# Revit family: 2M_Check Valve_UNIVAL_CHE-0601 - 125-200 mm
name_source: partatom
category: Pipe Accessories
revit_build: Autodesk Revit 2016 (Build: 20150220_1215(x64)
units: mm (PartAtom-declared; Revit-internal decimal feet)

## family parameters
Always vertical = Yes
Cut with Voids When Loaded = No
OmniClass Number = 23.65.55.14
OmniClass Title = Valves for Liquid Services
Part Type = Valve - Breaks Into
Round Connector Dimension = Use Diameter
Shared = No
Work Plane-Based = No

## types (3) — shared parameters
Body Material = Ductile iron / Stainless steel (GGG50)
Certifications = TSE, EAC, CE
Connection Type = Wafer
Description = Disk check valve
Description TR = Disk tipi çek vana
Disc Material = Ductile iron / Stainless steel (GGG50)
Guide Material = Ductile iron (GGG50)
Loss Method = Not Defined
Manufacturer = Giacomini Unival
Giacomini Unival
Giacomini Unival
Max. Working Temperature = 180°C
Pressure Rating = PN16
Spring Material = Stainless steel
Standard No = TS 1074
URL = http://www.unival.com.tr

## per-type parameters (varying)
| type | DN | L | L1 | Model | d | d1 | d2 |
| DN125 | 125 mm | 90 mm  [stored 0.295276 ft] | 18 mm  [stored 0.0590551 ft] | CHE-0601X125 | 184 mm  [stored 0.603675 ft] | 112 mm  [stored 0.367454 ft] | 180 mm |
| DN150 | 150 mm | 106 mm  [stored 0.347769 ft] | 21 mm | CHE-0601X150 | 209 mm  [stored 0.685696 ft] | 132 mm  [stored 0.433071 ft] | 205 mm |
| DN200 | 200 mm | 140 mm  [stored 0.459318 ft] | 28 mm  [stored 0.0918635 ft] | CHE-0601X200 | 264 mm  [stored 0.866142 ft] | 175 mm  [stored 0.574147 ft] | 259 mm |

note: [stored X ft] marks values corroborated as IEEE doubles in the binary element streams (Revit-internal decimal feet)

## geometry (parser evidence)
native form markers: Sweep x2
no freeform markers — native parametric forms only
